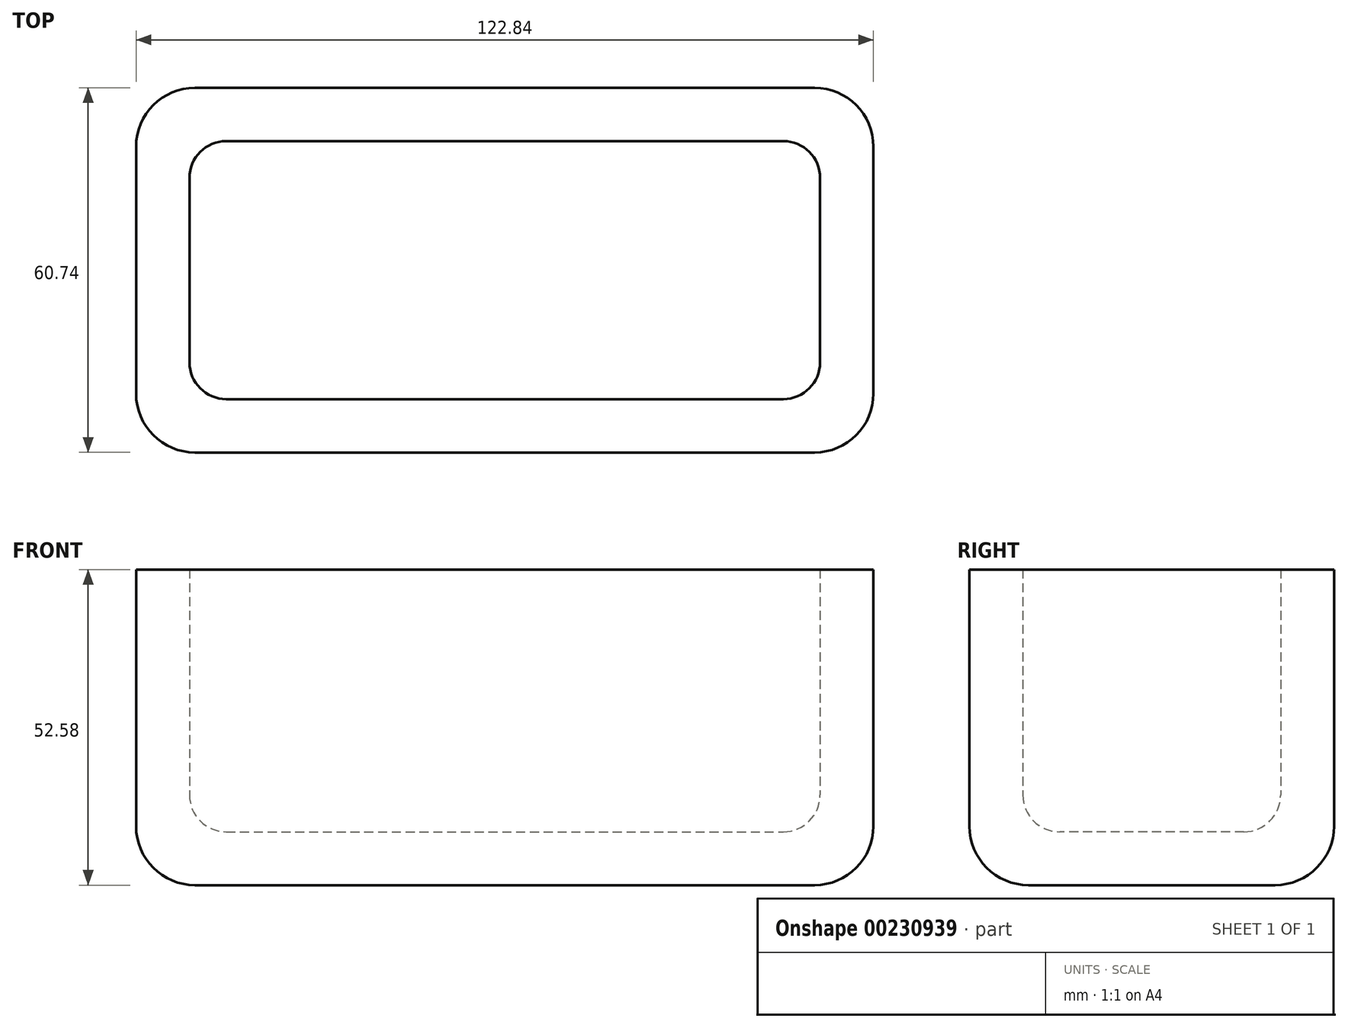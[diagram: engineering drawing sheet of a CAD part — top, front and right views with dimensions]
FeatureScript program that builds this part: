
annotation { "Feature Type Name" : "Feature", "Feature Type Description" : "" }
export const myFeature = defineFeature(function(context is Context, id is Id, definition is map)
    precondition{}
    {
        {
            var Q0;
            Q0=qCreatedBy(makeId("Top.planeOp"),FACE);
            var sketch = newSketch(context, id + "F0", { "sketchPlane" : qUnion([Q0])});
            skLineSegment(sketch, "E0.bottom", {"start": v(-59.38, 31.05) * mm, "end": v(63.46, 31.05) * mm});
            skLineSegment(sketch, "E0.top", {"start": v(-59.38, -29.7) * mm, "end": v(63.46, -29.7) * mm});
            skLineSegment(sketch, "E0.left", {"start": v(-59.38, 31.05) * mm, "end": v(-59.38, -29.7) * mm});
            skLineSegment(sketch, "E0.right", {"start": v(63.46, 31.05) * mm, "end": v(63.46, -29.7) * mm});
            skSolve(sketch);
        }
        {
            var Q0;
            Q0=makeQuery(id+"F0.imprint","IMPRINT",FACE,{"disambiguationData":[TD([[makeQuery(id+"F0.imprint","IMPRINT",EDGE,{"derivedFrom":sQuery(id+"F0.wireOp",EDGE,"E0.bottom")}),-1.0]])]});
            extrude(context, id + "F1", {"entities" : qUnion([Q0]), "depth" : 52.58 * mm});
        }
        {
            var Q0;
            Q0=makeQuery(id+"F1.opExtrude","CAP_FACE",FACE,{"disambiguationData":[OSD([sQuery(id+"F0.wireOp",EDGE,"E0.bottom"),sQuery(id+"F0.wireOp",EDGE,"E0.top"),sQuery(id+"F0.wireOp",EDGE,"E0.left"),sQuery(id+"F0.wireOp",EDGE,"E0.right")])],"isStart":false});
            shell(context, id + "F2", {"entities" : qUnion([Q0]), "thickness" : 8.9 * mm});
        }
        {
            var Q0;
            Q0=makeQuery(id+"F1.opExtrude","SWEPT_EDGE",EDGE,{"disambiguationData":[OSD([sQuery(id+"F0.wireOp",EDGE,"E0.top"),sQuery(id+"F0.wireOp",EDGE,"E0.left")])]});
            var Q1;
            Q1=makeQuery(id+"F1.opExtrude","CAP_EDGE",EDGE,{"disambiguationData":[OSD([sQuery(id+"F0.wireOp",EDGE,"E0.top")])],"isStart":true});
            var Q2;
            Q2=makeQuery(id+"F1.opExtrude","CAP_FACE",FACE,{"disambiguationData":[OSD([sQuery(id+"F0.wireOp",EDGE,"E0.bottom"),sQuery(id+"F0.wireOp",EDGE,"E0.top"),sQuery(id+"F0.wireOp",EDGE,"E0.left"),sQuery(id+"F0.wireOp",EDGE,"E0.right")])],"isStart":true});
            var Q3;
            Q3=makeQuery(id+"F1.opExtrude","SWEPT_EDGE",EDGE,{"disambiguationData":[OSD([sQuery(id+"F0.wireOp",EDGE,"E0.bottom"),sQuery(id+"F0.wireOp",EDGE,"E0.left")])]});
            var Q4;
            Q4=makeQuery(id+"F1.opExtrude","SWEPT_EDGE",EDGE,{"disambiguationData":[OSD([sQuery(id+"F0.wireOp",EDGE,"E0.bottom"),sQuery(id+"F0.wireOp",EDGE,"E0.right")])]});
            var Q5;
            Q5=makeQuery(id+"F1.opExtrude","SWEPT_EDGE",EDGE,{"disambiguationData":[OSD([sQuery(id+"F0.wireOp",EDGE,"E0.top"),sQuery(id+"F0.wireOp",EDGE,"E0.right")])]});
            fillet(context, id + "F3", {"entities" : qUnion([Q0, Q1, Q2, Q3, Q4, Q5]), "radius" : 9.8 * mm, "tangentPropagation" : true, "allowEdgeOverflow" : false});
        }
        {
            var Q0;
            Q0=makeQuery(id+"F2.opShell","OFFSET_FACE",FACE,{"disambiguationData":[OSD([sQuery(id+"F0.wireOp",EDGE,"E0.bottom"),sQuery(id+"F0.wireOp",EDGE,"E0.top"),sQuery(id+"F0.wireOp",EDGE,"E0.left"),sQuery(id+"F0.wireOp",EDGE,"E0.right")])]});
            var Q1;
            Q1=makeQuery(id+"F2.opShell","OFFSET_EDGE",EDGE,{"disambiguationData":[OSD([sQuery(id+"F0.wireOp",EDGE,"E0.top"),sQuery(id+"F0.wireOp",EDGE,"E0.left")])]});
            var Q2;
            Q2=makeQuery(id+"F2.opShell","OFFSET_EDGE",EDGE,{"disambiguationData":[OSD([sQuery(id+"F0.wireOp",EDGE,"E0.bottom"),sQuery(id+"F0.wireOp",EDGE,"E0.left")])]});
            var Q3;
            Q3=makeQuery(id+"F2.opShell","OFFSET_EDGE",EDGE,{"disambiguationData":[OSD([sQuery(id+"F0.wireOp",EDGE,"E0.top"),sQuery(id+"F0.wireOp",EDGE,"E0.right")])]});
            var Q4;
            Q4=makeQuery(id+"F2.opShell","OFFSET_EDGE",EDGE,{"disambiguationData":[OSD([sQuery(id+"F0.wireOp",EDGE,"E0.bottom"),sQuery(id+"F0.wireOp",EDGE,"E0.right")])]});
            fillet(context, id + "F4", {"entities" : qUnion([Q0, Q1, Q2, Q3, Q4]), "radius" : 6.13 * mm, "tangentPropagation" : true, "allowEdgeOverflow" : false});
        }
    });
